# Revit family: RN 13025 Sicherheitsgruppe Eckausführung
name_source: partatom
category: Rohrzubehör
units: mm (PartAtom-declared; Revit-internal decimal feet)

## family parameters
Arbeitsebenenbasiert = Nein
Beim Laden mit Abzugskörper schneiden = Nein
Bemaßung runder Anschluss = Durchmesser verwenden
Gemeinsam genutzt = Nein
Immer vertikal = Ja
Teiletyp = Ventil - Zerlegung in

## types (2) — shared parameters
1.010.00.2 Blattnummer der Richtlinie = 17
1.010.00.3 Ausgabedatum (Monat) der Richtlinie = 201601
1.010.00.4 Herstellername = R. Nussbaum AG
1.010.00.5 Revisionsdatum der Datei = 20190528
1.010.00.6 Webadresse des Herstellers = http://www.nussbaum.ch
1.100.00.3 Sortiernummer für Anzeigereihenfolge = 5
1.100.00.4 Produktbezeichnung = Sicherheitsarmaturen
1.960/3L.00.8 Link (URL) = https://www.nussbaum.ch
17.700.00.4 Armaturentyp = 6
17.700.00.7 Maximale Betriebstemperatur TB [°C] = 90
17.700.00.8 Maximaler Betriebsdruck (Arbeitsdruck) ps [1.0 · 105 Pa] = 10
CONNECTOR0_ref_dZ = 2 mm  [stored 0.00656168 ft]
CONNECTOR2_DIAMETER_dZ_0r = 20 mm
Connector Visibility = Nein
EnclosingSpace Visibility = Nein
Hersteller = R. Nussbauzm AG
URL = https://www.nussbaum.ch

## per-type parameters (varying)
- DN 15: 1.800.00.3 TGA-Nummer=00500500000000000000000000000200700000000000000001???00000; 1.810.00.3 Hersteller-Bestellnummer=13025.34; 1.810.00.4 DATANORM-Nummer=13025.34; 1.810.00.5 StLB-Nummer=612.113; 1.810.00.6 GTIN-Nummer=7612945001580; 17.700.00.30 Produktbeschreibung=13025.34, Sicherheitsgruppe Eckausführung, ohne Anschlussverschraubungen, DN=15,; 17.700.00.5 Nennweite DN=15; 17.700.00.6 kvs-Wert [m3/h]=1.8; CONNECTOR0_DIAMETER_dX_0r=20 mm; CONNECTOR0_dX_00=66 mm; CONNECTOR0_dX_01=57 mm; CONNECTOR0_ref_dX=66 mm; CONNECTOR1_DIAMETER_dZ_0r=20 mm; CONNECTOR1_dZ_00=26 mm; CONNECTOR1_dZ_01=34 mm; CONNECTOR1_ref_dX=17 mm; CONNECTOR1_ref_dZ=34 mm; CONNECTOR2_dZ_00=30 mm; CONNECTOR2_dZ_01=15 mm; CONNECTOR2_ref_dX=34 mm; CONNECTOR2_ref_dZ=15 mm; Modell=13025.34; R. Nussbaum AG 13025.34 de Visibility=Ja; R. Nussbaum AG 13025.35 de Visibility=Nein; Typenkommentare=Sicherheitsgruppe EckausführungDN 15
- DN 20: 1.800.00.3 TGA-Nummer=00500500000000000000000000000200700000000000000002???00000; 1.810.00.3 Hersteller-Bestellnummer=13025.35; 1.810.00.4 DATANORM-Nummer=13025.35; 1.810.00.5 StLB-Nummer=612.114; 1.810.00.6 GTIN-Nummer=7612945001597; 17.700.00.30 Produktbeschreibung=13025.35, Sicherheitsgruppe Eckausführung, ohne Anschlussverschraubungen, DN=20,; 17.700.00.5 Nennweite DN=20; 17.700.00.6 kvs-Wert [m3/h]=3.6; CONNECTOR0_DIAMETER_dX_0r=25 mm  [stored 0.082021 ft]; CONNECTOR0_dX_00=73 mm; CONNECTOR0_dX_01=63 mm; CONNECTOR0_ref_dX=73 mm; CONNECTOR1_DIAMETER_dZ_0r=25 mm  [stored 0.082021 ft]; CONNECTOR1_dZ_00=30 mm; CONNECTOR1_dZ_01=40 mm; CONNECTOR1_ref_dX=18 mm; CONNECTOR1_ref_dZ=40 mm; CONNECTOR2_dZ_00=35 mm; CONNECTOR2_dZ_01=20 mm; CONNECTOR2_ref_dX=37 mm; CONNECTOR2_ref_dZ=20 mm; Modell=13025.35; R. Nussbaum AG 13025.34 de Visibility=Nein; R. Nussbaum AG 13025.35 de Visibility=Ja; Typenkommentare=Sicherheitsgruppe EckausführungDN 20

note: [stored X ft] marks values corroborated as IEEE doubles in the binary element streams (Revit-internal decimal feet)

## geometry (parser evidence)
native form markers: Sweep x2
no freeform markers — native parametric forms only
